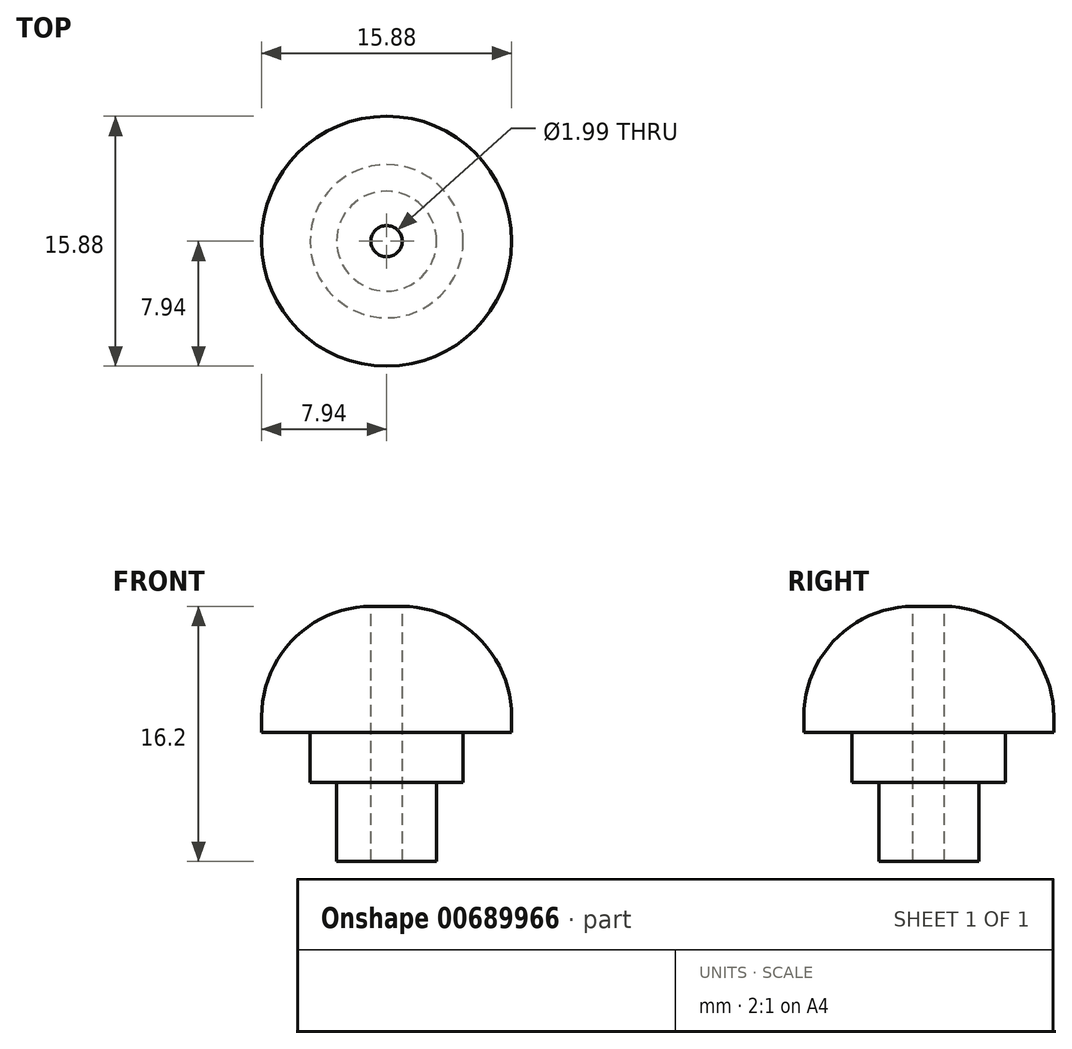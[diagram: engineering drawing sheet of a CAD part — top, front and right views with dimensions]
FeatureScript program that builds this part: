
annotation { "Feature Type Name" : "Feature", "Feature Type Description" : "" }
export const myFeature = defineFeature(function(context is Context, id is Id, definition is map)
    precondition{}
    {
        {
            var Q0;
            Q0=qCreatedBy(makeId("Top.planeOp"),FACE);
            var sketch = newSketch(context, id + "F0", { "sketchPlane" : qUnion([Q0])});
            skCircle(sketch, "E0", {"center": v(0, 0) * mm, "radius": 4.86 * mm});
            skSolve(sketch);
        }
        {
            var Q0;
            Q0=makeQuery(id+"F0.imprint","IMPRINT",FACE,{"disambiguationData":[TD([[makeQuery(id+"F0.imprint","IMPRINT",EDGE,{"derivedFrom":sQuery(id+"F0.wireOp",EDGE,"E0")}),1.0]])]});
            extrude(context, id + "F1", {"entities" : qUnion([Q0]), "depth" : 3.2 * mm, "offsetDistance" : 25 * mm});
        }
        {
            var Q0;
            Q0=makeQuery(id+"F1.opExtrude","CAP_FACE",FACE,{"disambiguationData":[OSD([sQuery(id+"F0.wireOp",EDGE,"E0"),sQuery(id+"F0.wireOp",EDGE,"7IkDOBrF-HAPB-mvcu-QDEx-u7b2h0kVA6eV")])],"isStart":false});
            var sketch = newSketch(context, id + "F2", { "sketchPlane" : qUnion([Q0])});
            skCircle(sketch, "E1", {"center": v(0, 0) * mm, "radius": 7.94 * mm});
            skSolve(sketch);
        }
        {
            var Q0;
            Q0=makeQuery(id+"F2.imprint","IMPRINT",FACE,{"disambiguationData":[TD([[makeQuery(id+"F2.imprint","IMPRINT",EDGE,{"derivedFrom":sQuery(id+"F2.wireOp",EDGE,"E1")}),1.0]])]});
            var Q1;
            Q1=makeQuery(id+"F2.imprint","IMPRINT",FACE,{"disambiguationData":[TD([[makeQuery(id+"F2.imprint","IMPRINT",EDGE,{"derivedFrom":makeQuery(id+"F1.opExtrude","CAP_EDGE",EDGE,{"disambiguationData":[OSD([sQuery(id+"F0.wireOp",EDGE,"E0")])],"isStart":false})}),1.0]])]});
            var Q2;
            Q2=sQuery(id+"F2.wireOp",EDGE,"E1");
            extrude(context, id + "F3", {"entities" : qUnion([Q0, Q1]), "operationType" : NewBodyOperationType.ADD, "surfaceEntities" : qUnion([Q2]), "depth" : 8 * mm, "offsetDistance" : 25 * mm});
        }
        {
            var Q0;
            Q0=makeQuery(id+"F3.opExtrude","CAP_EDGE",EDGE,{"disambiguationData":[OSD([sQuery(id+"F2.wireOp",EDGE,"E1")])],"isStart":false});
            fillet(context, id + "F4", {"entities" : qUnion([Q0]), "radius" : 7 * mm, "tangentPropagation" : true, "allowEdgeOverflow" : false});
        }
        {
            var Q0;
            Q0=qCreatedBy(makeId("Top.planeOp"),FACE);
            var sketch = newSketch(context, id + "F5", { "sketchPlane" : qUnion([Q0])});
            skCircle(sketch, "E2", {"center": v(0, 0) * mm, "radius": 3.18 * mm});
            skSolve(sketch);
        }
        {
            var Q0;
            Q0=makeQuery(id+"F5.imprint","IMPRINT",FACE,{"disambiguationData":[TD([[makeQuery(id+"F5.imprint","IMPRINT",EDGE,{"derivedFrom":sQuery(id+"F5.wireOp",EDGE,"E2")}),1.0]])]});
            extrude(context, id + "F6", {"entities" : qUnion([Q0]), "operationType" : NewBodyOperationType.ADD, "oppositeDirection" : true, "depth" : 5 * mm, "offsetDistance" : 25 * mm});
        }
        {
            var Q0;
            Q0=qCreatedBy(makeId("Top.planeOp"),FACE);
            var sketch = newSketch(context, id + "F7", { "sketchPlane" : qUnion([Q0])});
            skCircle(sketch, "E3", {"center": v(0, 0) * mm, "radius": 1 * mm});
            skSolve(sketch);
        }
        {
            var Q0;
            Q0 = qSketchRegion(id + "F7", true);
            extrude(context, id + "F8", {"entities" : qUnion([Q0]), "operationType" : NewBodyOperationType.REMOVE, "oppositeDirection" : true, "depth" : 25 * mm, "offsetDistance" : 25 * mm, "hasSecondDirection" : true, "secondDirectionOppositeDirection" : false, "secondDirectionDepth" : 25 * mm});
        }
    });
